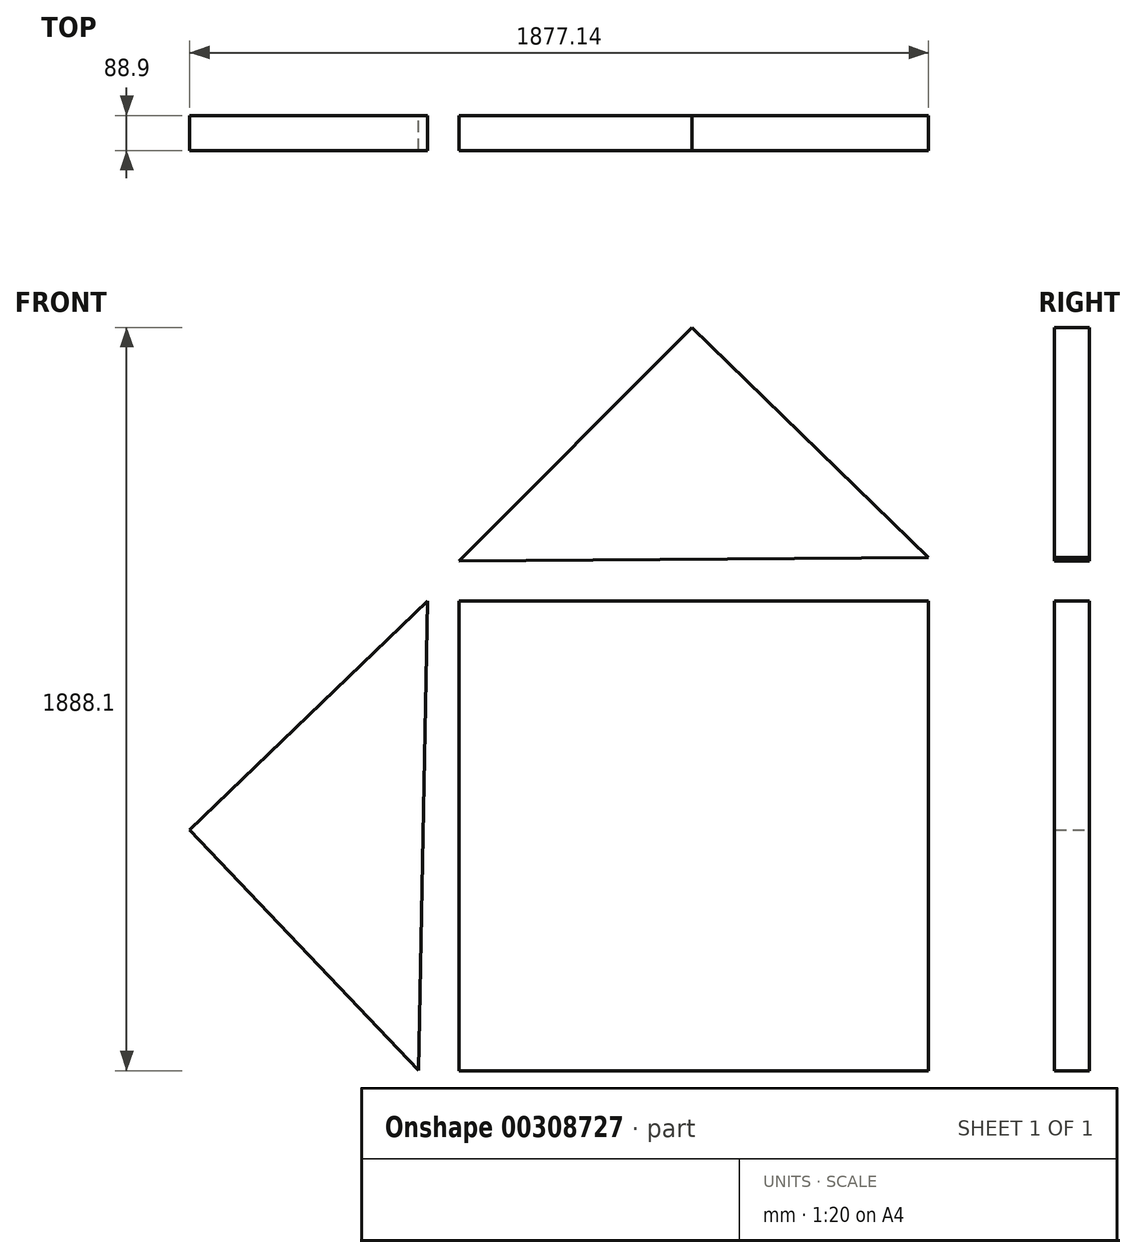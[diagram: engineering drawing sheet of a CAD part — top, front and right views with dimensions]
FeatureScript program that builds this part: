
annotation { "Feature Type Name" : "Feature", "Feature Type Description" : "" }
export const myFeature = defineFeature(function(context is Context, id is Id, definition is map)
    precondition{}
    {
        {
            var Q0;
            Q0=qCreatedBy(makeId("Front.planeOp"),FACE);
            var sketch = newSketch(context, id + "F0", { "sketchPlane" : qUnion([Q0])});
            skLineSegment(sketch, "E0.bottom", {"start": v(-788.98, 581.74) * mm, "end": v(404.82, 581.74) * mm});
            skLineSegment(sketch, "E0.top", {"start": v(-788.98, -612.06) * mm, "end": v(404.82, -612.06) * mm});
            skLineSegment(sketch, "E0.left", {"start": v(-788.98, 581.74) * mm, "end": v(-788.98, -612.06) * mm});
            skLineSegment(sketch, "E0.right", {"start": v(404.82, 581.74) * mm, "end": v(404.82, -612.06) * mm});
            skSolve(sketch);
        }
        {
            var Q0;
            Q0=makeQuery(id+"F0.imprint","IMPRINT",FACE,{"disambiguationData":[TD([[makeQuery(id+"F0.imprint","IMPRINT",EDGE,{"derivedFrom":sQuery(id+"F0.wireOp",EDGE,"E0.bottom")}),-1.0]])]});
            extrude(context, id + "F1", {"entities" : qUnion([Q0]), "depth" : 88.9 * mm});
        }
        {
            var Q0;
            Q0=qCreatedBy(makeId("Front.planeOp"),FACE);
            var sketch = newSketch(context, id + "F2", { "sketchPlane" : qUnion([Q0])});
            skLineSegment(sketch, "E1.left", {"start": v(-868.87, 581.74) * mm, "end": v(-890.73, -611.86) * mm});
            skLineSegment(sketch, "E2", {"start": v(-868.87, 581.74) * mm, "end": v(-1472.32, 0) * mm});
            skLineSegment(sketch, "E3", {"start": v(-1472.32, 0) * mm, "end": v(-890.73, -611.86) * mm});
            skSolve(sketch);
        }
        {
            var Q0;
            Q0=makeQuery(id+"F2.imprint","IMPRINT",FACE,{"disambiguationData":[TD([[makeQuery(id+"F2.imprint","IMPRINT",EDGE,{"derivedFrom":sQuery(id+"F2.wireOp",EDGE,"E1.left")}),-1.0]])]});
            extrude(context, id + "F3", {"entities" : qUnion([Q0]), "depth" : 88.9 * mm});
        }
        {
            var Q0;
            Q0=qCreatedBy(makeId("Front.planeOp"),FACE);
            var sketch = newSketch(context, id + "F4", { "sketchPlane" : qUnion([Q0])});
            skLineSegment(sketch, "E4.left", {"start": v(404.8, 691.84) * mm, "end": v(-788.98, 683.34) * mm});
            skLineSegment(sketch, "E5", {"start": v(404.8, 691.84) * mm, "end": v(-196.28, 1276.04) * mm});
            skLineSegment(sketch, "E6", {"start": v(-196.28, 1276.04) * mm, "end": v(-788.98, 683.34) * mm});
            skSolve(sketch);
        }
        {
            var Q0;
            Q0=makeQuery(id+"F4.imprint","IMPRINT",FACE,{"disambiguationData":[TD([[makeQuery(id+"F4.imprint","IMPRINT",EDGE,{"derivedFrom":sQuery(id+"F4.wireOp",EDGE,"E4.left")}),-1.0]])]});
            extrude(context, id + "F5", {"entities" : qUnion([Q0]), "depth" : 88.9 * mm});
        }
    });
